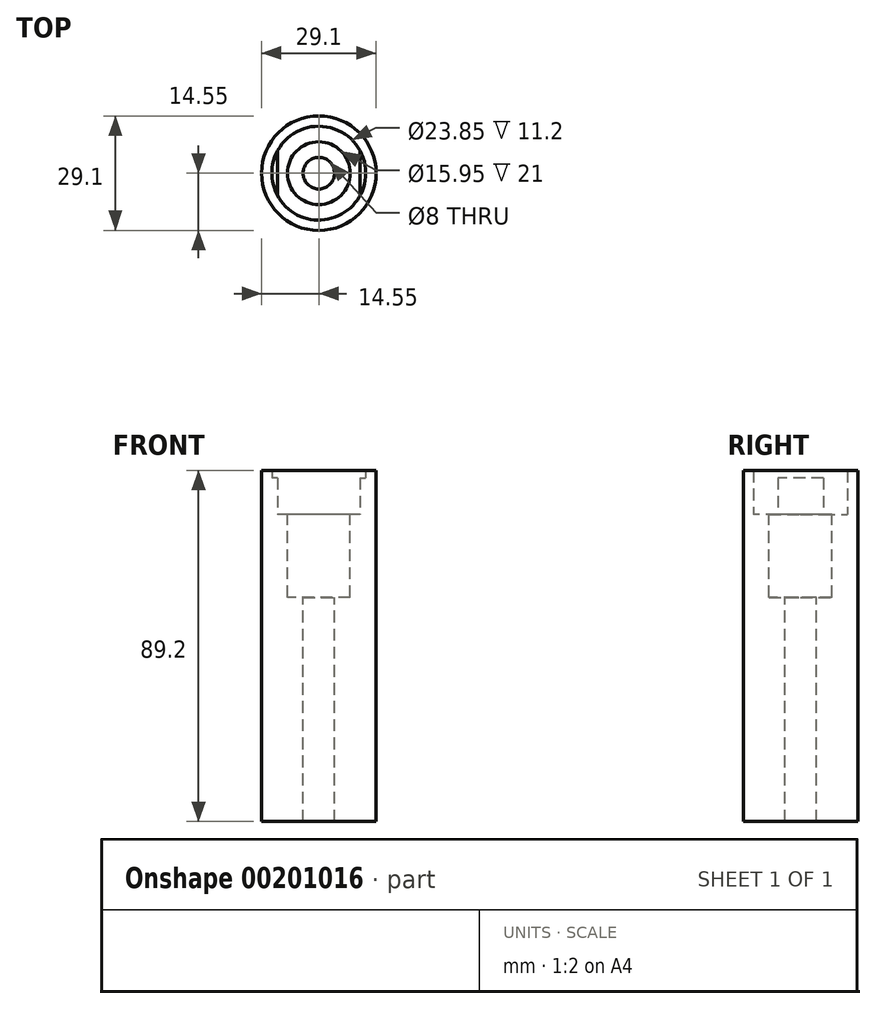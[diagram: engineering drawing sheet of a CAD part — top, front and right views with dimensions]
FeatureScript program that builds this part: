
annotation { "Feature Type Name" : "Feature", "Feature Type Description" : "" }
export const myFeature = defineFeature(function(context is Context, id is Id, definition is map)
    precondition{}
    {
        {
            var Q0;
            Q0=qCreatedBy(makeId("Top.planeOp"),FACE);
            var sketch = newSketch(context, id + "F0", { "sketchPlane" : qUnion([Q0])});
            skArc(sketch, "E0", {"start": v(-10.43, -5.8) * mm, "mid": v(0, -11.93) * mm, "end": v(10.43, -5.8) * mm});
            skCircle(sketch, "E1", {"center": v(0, 0) * mm, "radius": 14.55 * mm});
            skCircle(sketch, "E2", {"center": v(0, 0) * mm, "radius": 7.97 * mm});
            skLineSegment(sketch, "E3", {"start": v(-10.43, 5.8) * mm, "end": v(-10.43, -5.8) * mm});
            skLineSegment(sketch, "E4.MirrorCS", {"start": v(10.43, 5.8) * mm, "end": v(10.43, -5.8) * mm});
            skArc(sketch, "E5.trimOffspring", {"start": v(10.42, 5.8) * mm, "mid": v(0, 11.92) * mm, "end": v(-10.42, 5.8) * mm});
            skArc(sketch, "E6", {"start": v(-10.43, 5.8) * mm, "mid": v(-11.93, 0) * mm, "end": v(-10.43, -5.8) * mm});
            skArc(sketch, "E7.MirrorCS", {"start": v(10.43, 5.8) * mm, "mid": v(11.93, 0) * mm, "end": v(10.43, -5.8) * mm});
            skSolve(sketch);
        }
        {
            var Q0;
            Q0=makeQuery(id+"F0.imprint","IMPRINT",FACE,{"disambiguationData":[TD([[makeQuery(id+"F0.imprint","IMPRINT",EDGE,{"derivedFrom":sQuery(id+"F0.wireOp",EDGE,"E0")}),-1.0]])]});
            extrude(context, id + "F1", {"entities" : qUnion([Q0]), "depth" : 11.2 * mm});
        }
        {
            var Q0;
            Q0=makeQuery(id+"F0.imprint","IMPRINT",FACE,{"disambiguationData":[TD([[makeQuery(id+"F0.imprint","IMPRINT",EDGE,{"derivedFrom":sQuery(id+"F0.wireOp",EDGE,"E3")}),-1.0]])]});
            var Q1;
            Q1=makeQuery(id+"F0.imprint","IMPRINT",FACE,{"disambiguationData":[TD([[makeQuery(id+"F0.imprint","IMPRINT",EDGE,{"derivedFrom":sQuery(id+"F0.wireOp",EDGE,"E4.MirrorCS")}),1.0]])]});
            extrude(context, id + "F2", {"entities" : qUnion([Q0, Q1]), "operationType" : NewBodyOperationType.ADD, "depth" : 9.35 * mm});
        }
        {
            var Q0;
            Q0=makeQuery(id+"F0.imprint","IMPRINT",FACE,{"disambiguationData":[TD([[makeQuery(id+"F0.imprint","IMPRINT",EDGE,{"derivedFrom":sQuery(id+"F0.wireOp",EDGE,"E0")}),1.0]])]});
            var Q1;
            Q1=makeQuery(id+"F0.imprint","IMPRINT",FACE,{"disambiguationData":[TD([[makeQuery(id+"F0.imprint","IMPRINT",EDGE,{"derivedFrom":sQuery(id+"F0.wireOp",EDGE,"E4.MirrorCS")}),1.0]])]});
            var Q2;
            Q2=makeQuery(id+"F0.imprint","IMPRINT",FACE,{"disambiguationData":[TD([[makeQuery(id+"F0.imprint","IMPRINT",EDGE,{"derivedFrom":sQuery(id+"F0.wireOp",EDGE,"E0")}),-1.0]])]});
            var Q3;
            Q3=makeQuery(id+"F0.imprint","IMPRINT",FACE,{"disambiguationData":[TD([[makeQuery(id+"F0.imprint","IMPRINT",EDGE,{"derivedFrom":sQuery(id+"F0.wireOp",EDGE,"E3")}),-1.0]])]});
            extrude(context, id + "F3", {"entities" : qUnion([Q0, Q1, Q2, Q3]), "operationType" : NewBodyOperationType.ADD, "oppositeDirection" : true, "depth" : 21 * mm});
        }
        {
            var Q0;
            Q0=makeQuery(id+"F3.opExtrude","CAP_FACE",FACE,{"disambiguationData":[OSD([sQuery(id+"F0.wireOp",EDGE,"E1"),sQuery(id+"F0.wireOp",EDGE,"E2")])],"isStart":false});
            var sketch = newSketch(context, id + "F4", { "sketchPlane" : qUnion([Q0])});
            skCircle(sketch, "E8.0", {"center": v(0, 0) * mm, "radius": 14.55 * mm});
            skCircle(sketch, "E9", {"center": v(0, 0) * mm, "radius": 4 * mm});
            skSolve(sketch);
        }
        {
            var Q0;
            Q0 = qSketchRegion(id + "F4", true);
            extrude(context, id + "F5", {"entities" : qUnion([Q0]), "operationType" : NewBodyOperationType.ADD, "depth" : 57 * mm});
        }
    });
